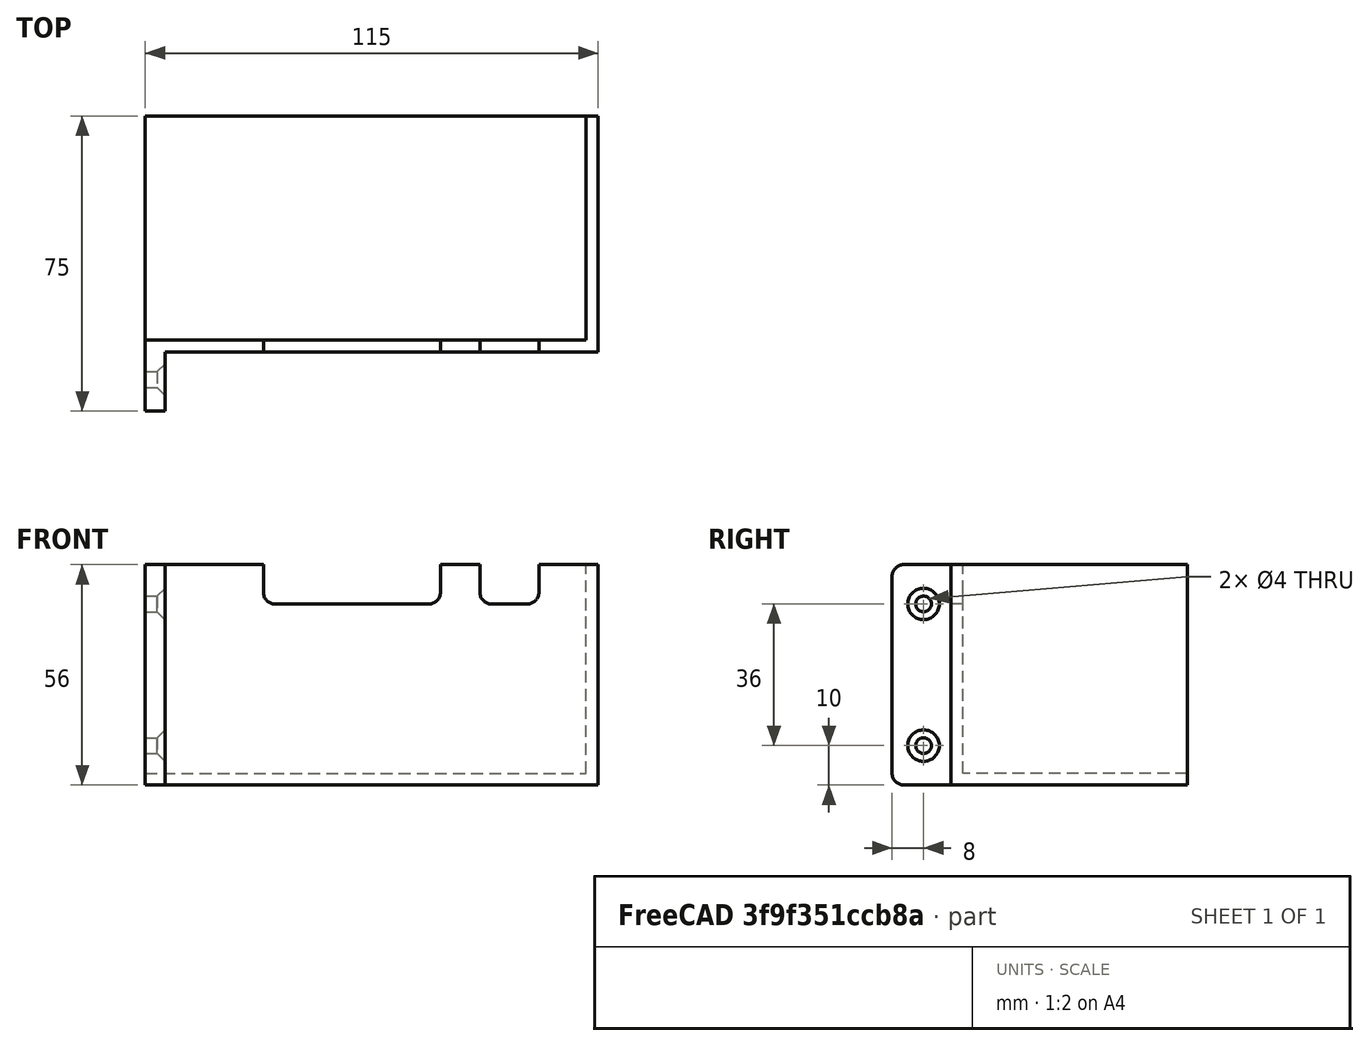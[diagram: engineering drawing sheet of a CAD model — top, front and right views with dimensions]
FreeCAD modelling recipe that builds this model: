
FCSTD DOCUMENT  (FreeCAD 0.14R3700 (Git))
Label: psu cover
License: CC-BY 3.0
LicenseURL: http://creativecommons.org/licenses/by/3.0/
objects: Part::Box×5, Part::Cut×4, Part::MultiFuse×4, Part::Fillet×2, Part::Cone×1, Part::Cylinder×1
note: 17 computed .brp shape members not serialized (recipe doc carries the construction recipe); baked Part::Feature solids carry a one-line shape summary decoded from their .brp

FEATURE [Part::Box] Box  label="Cube"
  Height = 60
  Length = 115
  Width = 56
FEATURE [Part::Box] Box001  label="Cube001"
  Height = 57
  Length = 112
  Placement = pos=(0,3,0) rot=(0,0,1;0rad)
  Width = 53
FEATURE [Part::Cut] Cut
  Base = -> Box
  Tool = -> Box001
FEATURE [Part::Box] Box002  label="mount"
  Height = 15
  Length = 5
  Placement = pos=(0,0,60) rot=(0,0,1;0rad)
  Width = 56
FEATURE [Part::Box] Box003  label="cablecutout"
  Height = 10
  Length = 70
  Placement = pos=(30,46,51) rot=(0,0,1;0rad)
  Width = 10
FEATURE [Part::Fillet] Fillet001
  Base = -> Box002
  Edges = 2 edges r=3: [Edge10,Edge12]
FEATURE [Part::MultiFuse] Fusion
  Shapes = -> [Fillet001,Cut]
FEATURE [Part::Box] Box004  label="cablecutout001"
  Height = 10
  Length = 10
  Placement = pos=(75,46,51) rot=(0,0,1;0rad)
  Width = 10
FEATURE [Part::Cut] Cut002
  Base = -> Box003
  Tool = -> Box004
FEATURE [Part::Fillet] Fillet
  Base = -> Cut002
  Edges = 4 edges r=3: [Edge1,Edge6,Edge13,Edge19]
FEATURE [Part::Cut] Cut003
  Base = -> Fusion
  Tool = -> Fillet
FEATURE [Part::Cone] Cone
  Angle = 360
  Height = 2
  Placement = pos=(0,0,10) rot=(0,0,1;0rad)
  Radius1 = 2
  Radius2 = 4
FEATURE [Part::Cylinder] Cylinder
  Angle = 360
  Height = 10
  Radius = 2
FEATURE [Part::MultiFuse] Fusion001  label="screw cutout"
  Placement = pos=(-7,46,67) rot=(0,1,0;1.5708rad)
  Shapes = -> [Cylinder,Cone]
FEATURE [Part::MultiFuse] Fusion002  label="screw cutout001"
  Placement = pos=(-7,10,67) rot=(0,1,0;1.5708rad)
  Shapes = -> [Cylinder,Cone]
FEATURE [Part::MultiFuse] Fusion003
  Shapes = -> [Fusion001,Fusion002]
FEATURE [Part::Cut] Cut004
  Base = -> Cut003
  Placement = pos=(0,0,0) rot=(1,0,0;1.5708rad)
  Tool = -> Fusion003
